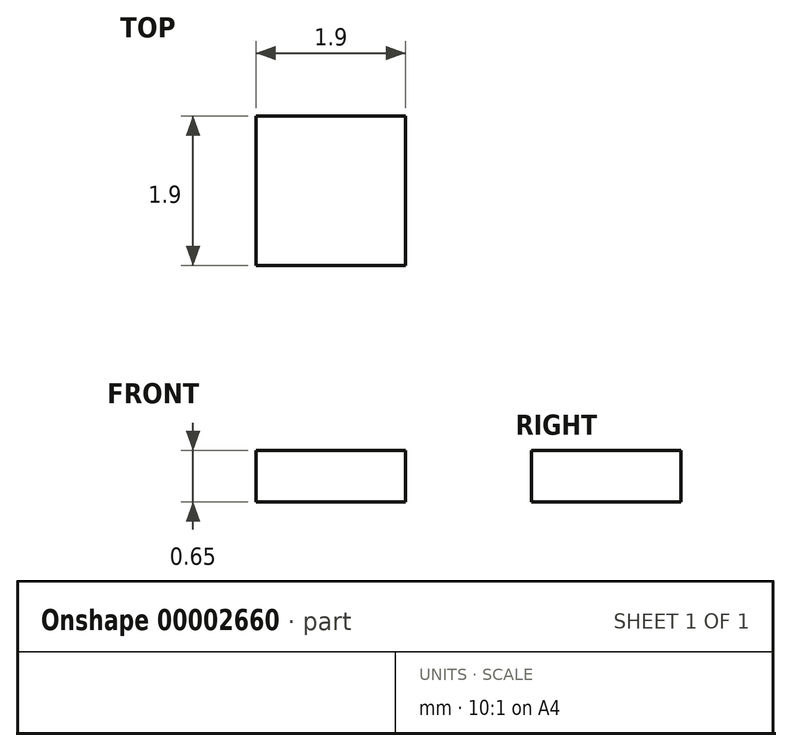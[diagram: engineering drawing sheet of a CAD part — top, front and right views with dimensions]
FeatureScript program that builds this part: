
annotation { "Feature Type Name" : "Feature", "Feature Type Description" : "" }
export const myFeature = defineFeature(function(context is Context, id is Id, definition is map)
    precondition{}
    {
        {
            var Q0;
            Q0=qCreatedBy(makeId("Top.planeOp"),FACE);
            var sketch = newSketch(context, id + "F0", { "sketchPlane" : qUnion([Q0])});
            skLineSegment(sketch, "E0.bottom", {"start": v(0.28, 1.37) * mm, "end": v(2.18, 1.37) * mm});
            skLineSegment(sketch, "E0.top", {"start": v(0.28, -0.53) * mm, "end": v(2.18, -0.53) * mm});
            skLineSegment(sketch, "E0.left", {"start": v(0.28, 1.37) * mm, "end": v(0.28, -0.53) * mm});
            skLineSegment(sketch, "E0.right", {"start": v(2.18, 1.37) * mm, "end": v(2.18, -0.53) * mm});
            skSolve(sketch);
        }
        {
            var Q0;
            Q0=makeQuery(id+"F0.imprint","IMPRINT",FACE,{"disambiguationData":[TD([[makeQuery(id+"F0.imprint","IMPRINT",EDGE,{"derivedFrom":sQuery(id+"F0.wireOp",EDGE,"E0.bottom")}),-1.0]])]});
            extrude(context, id + "F1", {"entities" : qUnion([Q0]), "depth" : .65 * mm});
        }
    });
